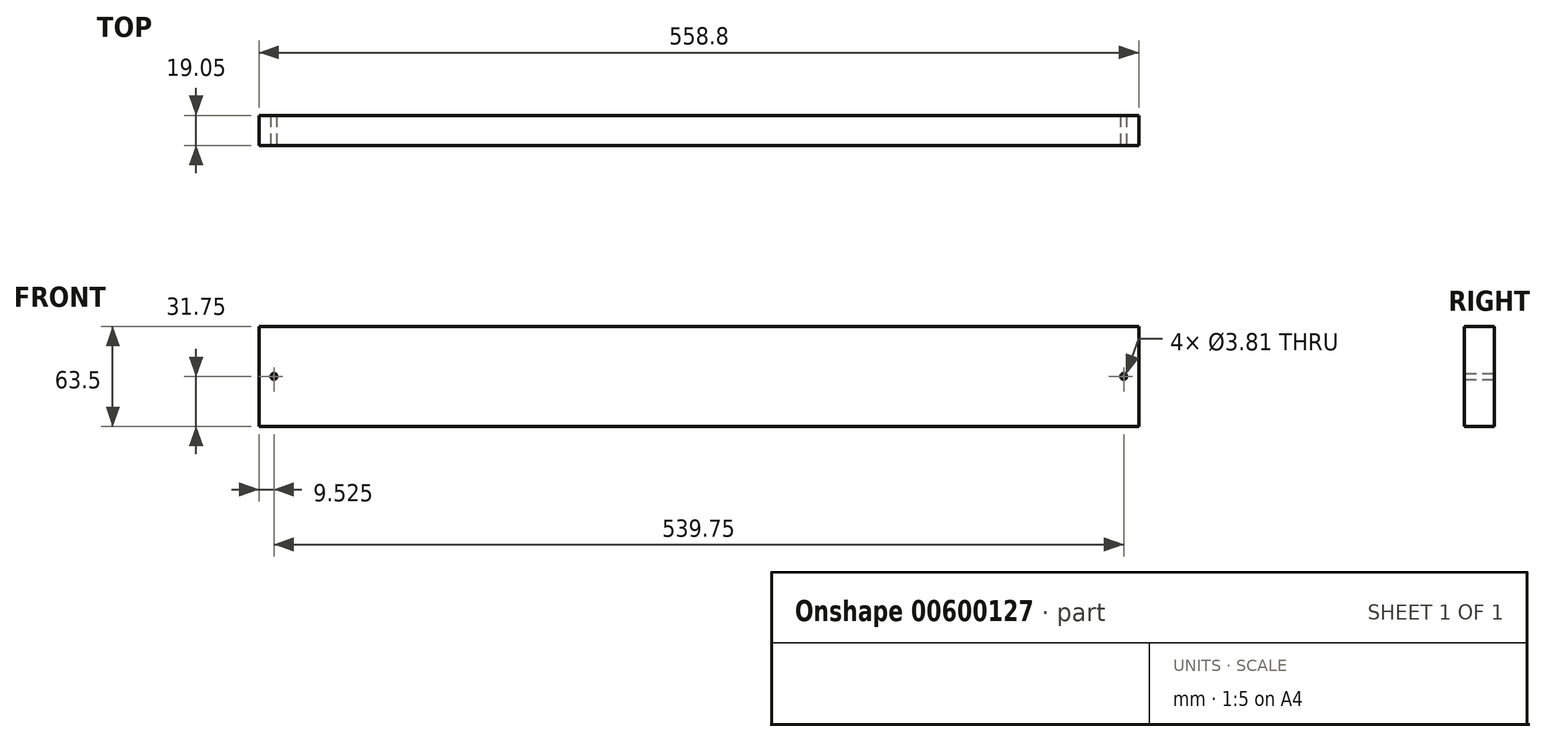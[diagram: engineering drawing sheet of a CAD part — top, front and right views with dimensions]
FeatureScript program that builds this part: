
annotation { "Feature Type Name" : "Feature", "Feature Type Description" : "" }
export const myFeature = defineFeature(function(context is Context, id is Id, definition is map)
    precondition{}
    {
        {
            var Q0;
            Q0=qCreatedBy(makeId("Front.planeOp"),FACE);
            var sketch = newSketch(context, id + "F0", { "sketchPlane" : qUnion([Q0])});
            skLineSegment(sketch, "E0.bottom", {"start": v(0, 0) * mm, "end": v(-558.8, 0) * mm});
            skLineSegment(sketch, "E0.top", {"start": v(0, 63.5) * mm, "end": v(-558.8, 63.5) * mm});
            skLineSegment(sketch, "E0.left", {"start": v(0, 0) * mm, "end": v(0, 63.5) * mm});
            skLineSegment(sketch, "E0.right", {"start": v(-558.8, 0) * mm, "end": v(-558.8, 63.5) * mm});
            skPoint(sketch, "E1.start.orphan", {"position": v(-558.8, 31.75) * mm});
            skLineSegment(sketch, "E2", {"start": v(-558.8, 31.75) * mm, "end": v(-549.28, 31.75) * mm, "construction": true});
            skLineSegment(sketch, "E3", {"start": v(-549.28, 31.75) * mm, "end": v(-9.53, 31.75) * mm, "construction": true});
            skLineSegment(sketch, "E4", {"start": v(-9.53, 31.75) * mm, "end": v(0, 31.75) * mm, "construction": true});
            skCircle(sketch, "E5", {"center": v(-549.28, 31.75) * mm, "radius": 1.9 * mm});
            skCircle(sketch, "E6", {"center": v(-9.53, 31.75) * mm, "radius": 1.9 * mm});
            skSolve(sketch);
        }
        {
            var Q0;
            Q0=makeQuery(id+"F0.imprint","IMPRINT",FACE,{"disambiguationData":[TD([[makeQuery(id+"F0.imprint","IMPRINT",EDGE,{"derivedFrom":sQuery(id+"F0.wireOp",EDGE,"E0.bottom")}),-1.0]])]});
            extrude(context, id + "F1", {"entities" : qUnion([Q0]), "depth" : 19.05 * mm, "offsetDistance" : 25.4 * mm});
        }
    });
